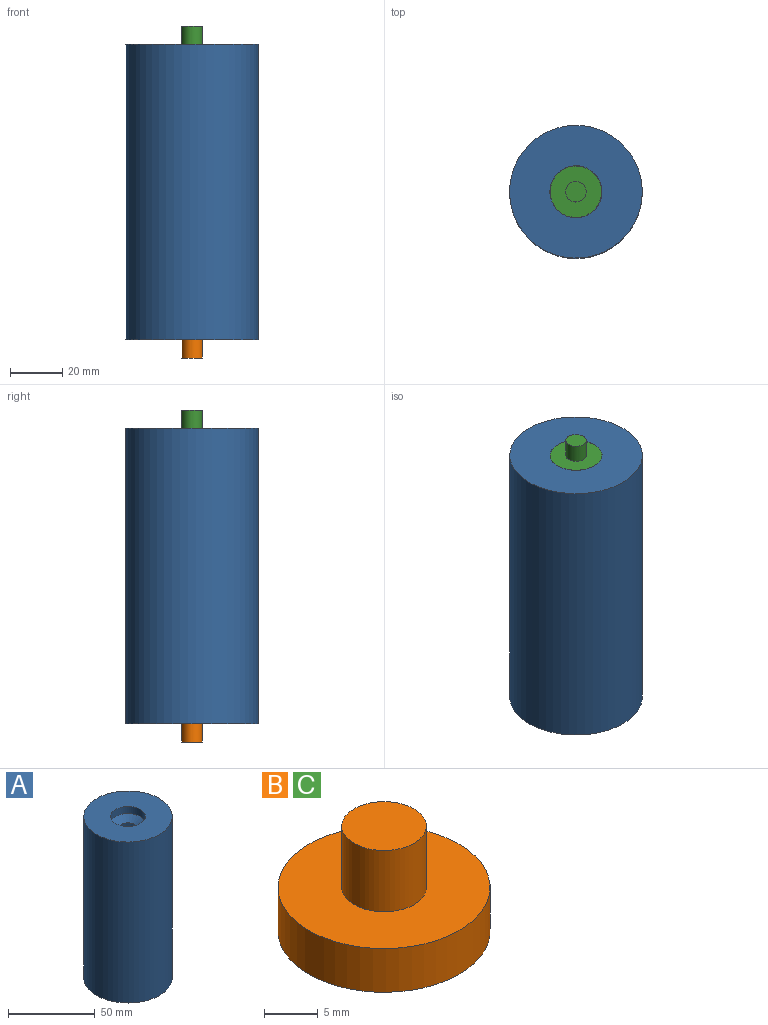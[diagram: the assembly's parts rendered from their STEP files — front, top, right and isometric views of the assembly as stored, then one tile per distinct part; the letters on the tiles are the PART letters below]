
ASSEMBLY  parts=3 mates=2
PART A: 10 faces, bbox 51x51x113.6 mm
  f0: plane 45x45mm, normal (0,0,1), area 1511.7mm2, adj f2,f4
  f1: plane 51x51mm, normal (0,0,-1), area 1728.7mm2, adj f3,f5
  f2: cone r=0mm half-angle=59deg, axis (0,0,-1), area 274.6mm2, adj f0,f3
  f3: cylinder r=10mm len=20mm, axis (0,0,-1), area 314.2mm2, adj f1,f2
  f4: cylinder r=22.5mm len=97.6mm, axis (0,0,-1), area 13797.9mm2, adj f0,f7
  f5: cylinder r=25.5mm len=113.6mm, axis (0,0,-1), area 18201.1mm2, adj f1,f6
  f6: plane 51x51mm, normal (0,0,1), area 1728.7mm2, adj f5,f9
  f7: plane 45x45mm, normal (0,0,-1), area 1511.7mm2, adj f4,f8
  f8: cone r=0mm half-angle=59deg, axis (0,0,1), area 274.6mm2, adj f7,f9
  f9: cylinder r=10mm len=20mm, axis (0,0,1), area 314.2mm2, adj f6,f8
PART B: 5 faces, bbox 19.8x19.8x12 mm
  f0: cylinder r=9.9mm len=19.8mm, axis (0,0,-1), area 311mm2, adj f1,f2
  f1: plane 19.8x19.8mm, normal (0,0,1), area 258.9mm2, adj f0,f3
  f2: plane 19.8x19.8mm, normal (0,0,-1), area 307.9mm2, adj f0
  f3: cylinder r=3.95mm len=7.9mm, axis (0,0,-1), area 173.7mm2, adj f1,f4
  f4: plane 7.9x7.9mm, normal (0,0,1), area 49mm2, adj f3
PART C: same geometry as B
PLACE A t=(-147.19,-119.97,90.36)mm fixed
PLACE B rot(axis=(1,0,0),180deg) t=(-147.19,-119.97,38.56)mm
PLACE C rot(axis=(0,0,-1),28.1deg) t=(-147.19,-119.97,142.16)mm
MATE revolute B.f0 <-> A.f2  axis (0,0,1) through (-147.19,-119.97,38.56)mm
MATE revolute C.f0 <-> A.f5  axis (0,0,-1) through (-147.19,-119.97,142.16)mm
